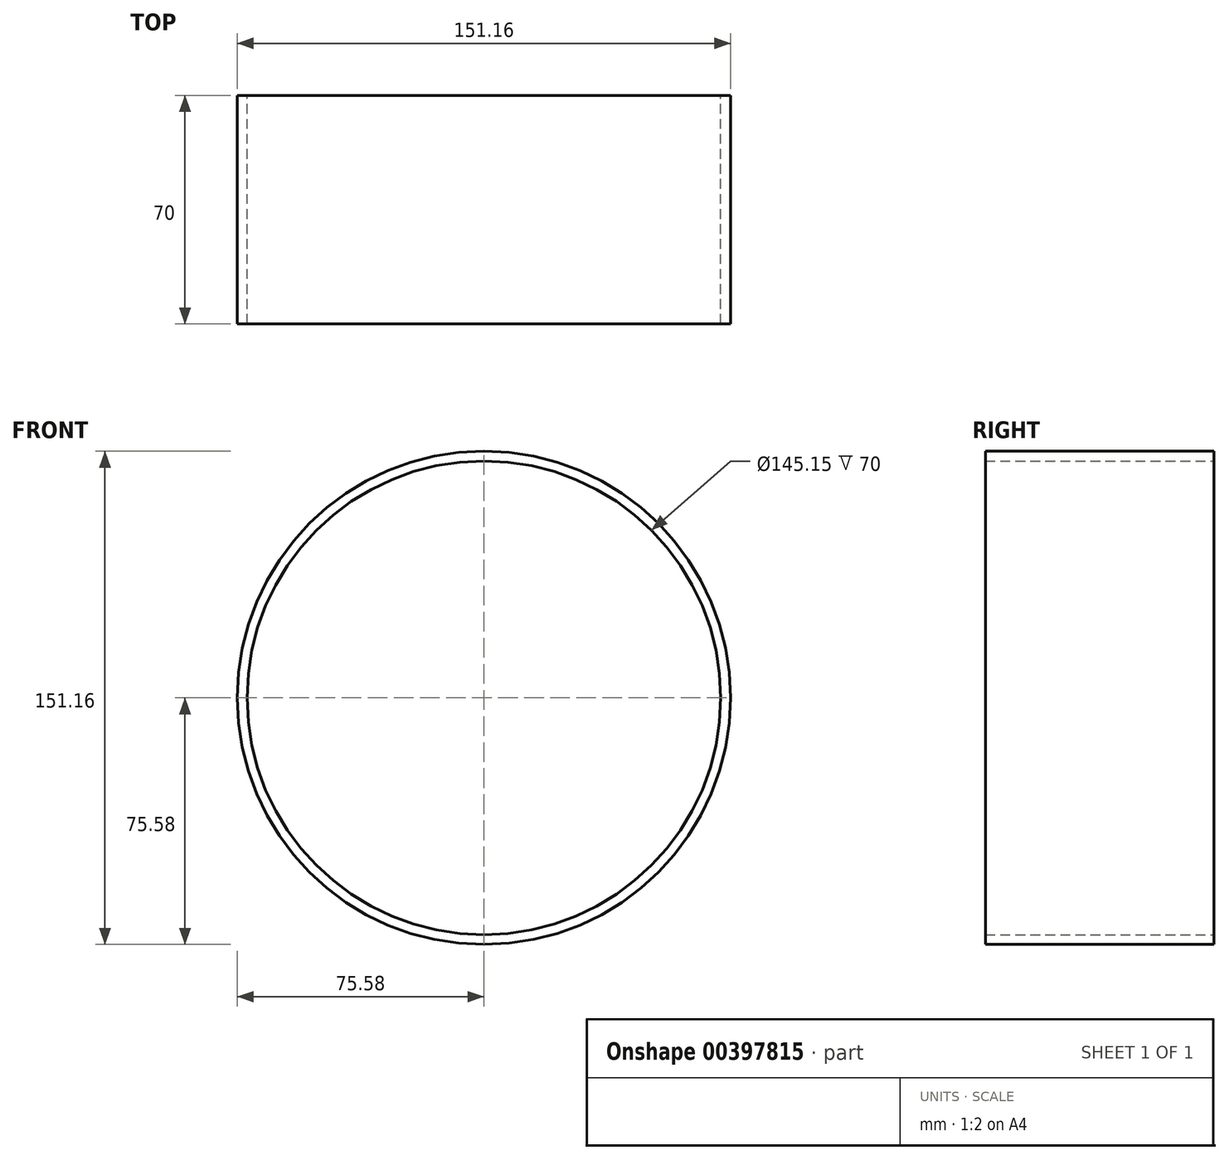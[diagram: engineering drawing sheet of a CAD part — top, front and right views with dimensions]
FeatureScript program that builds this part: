
annotation { "Feature Type Name" : "Feature", "Feature Type Description" : "" }
export const myFeature = defineFeature(function(context is Context, id is Id, definition is map)
    precondition{}
    {
        {
            var Q0;
            Q0=qCreatedBy(makeId("Front.planeOp"),FACE);
            var sketch = newSketch(context, id + "F0", { "sketchPlane" : qUnion([Q0])});
            skCircle(sketch, "E0", {"center": v(0, 0) * mm, "radius": 72.58 * mm});
            skCircle(sketch, "E1", {"center": v(0, 0) * mm, "radius": 75.58 * mm});
            skPoint(sketch, "E2.left.start.orphan", {"position": v(-72.58, 0) * mm});
            skPoint(sketch, "E3.right.start.orphan", {"position": v(-50, 52.6) * mm});
            skPoint(sketch, "E3.left.start.orphan", {"position": v(50, 52.6) * mm});
            skPoint(sketch, "E3.top.end.orphan", {"position": v(-50, -52.6) * mm});
            skPoint(sketch, "E3.top.start.orphan", {"position": v(50, -52.6) * mm});
            skSolve(sketch);
        }
        {
            var Q0;
            Q0=makeQuery(id+"F0.imprint","IMPRINT",FACE,{"disambiguationData":[TD([[makeQuery(id+"F0.imprint","IMPRINT",EDGE,{"derivedFrom":sQuery(id+"F0.wireOp",EDGE,"E0")}),-1.0]])]});
            extrude(context, id + "F1", {"entities" : qUnion([Q0]), "depth" : 70 * mm});
        }
    });
